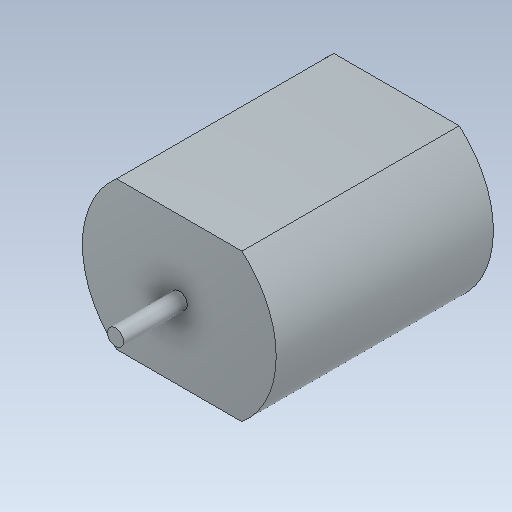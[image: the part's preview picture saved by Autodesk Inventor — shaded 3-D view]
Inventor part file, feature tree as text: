
AUTODESK INVENTOR PART (.ipt)
format: ipt  version: 2020 (Build 240168000, 168)  size: 113,664 bytes
history: native  units: mm
features: extrude x2, sketch x2
ambient origin geometry x8: Origin, YZ Plane, XZ Plane, XY Plane, X Axis, Y Axis, Z Axis, Center Point
bodies: Solid1 (feature_tree)
feature tree (4):
  extrude  "Extrusion1"  Depth=26.9mm
  extrude  "Extrusion2"  Depth=18.3mm
  sketch  "Sketch1"  dims[d0=17.3mm d2=26.9mm d3=0.0mm d4=2.0mm]
  sketch  "Sketch2"  dims[d5=7.9mm d6=0.0mm d7=24.0mm d8=18.3mm]
